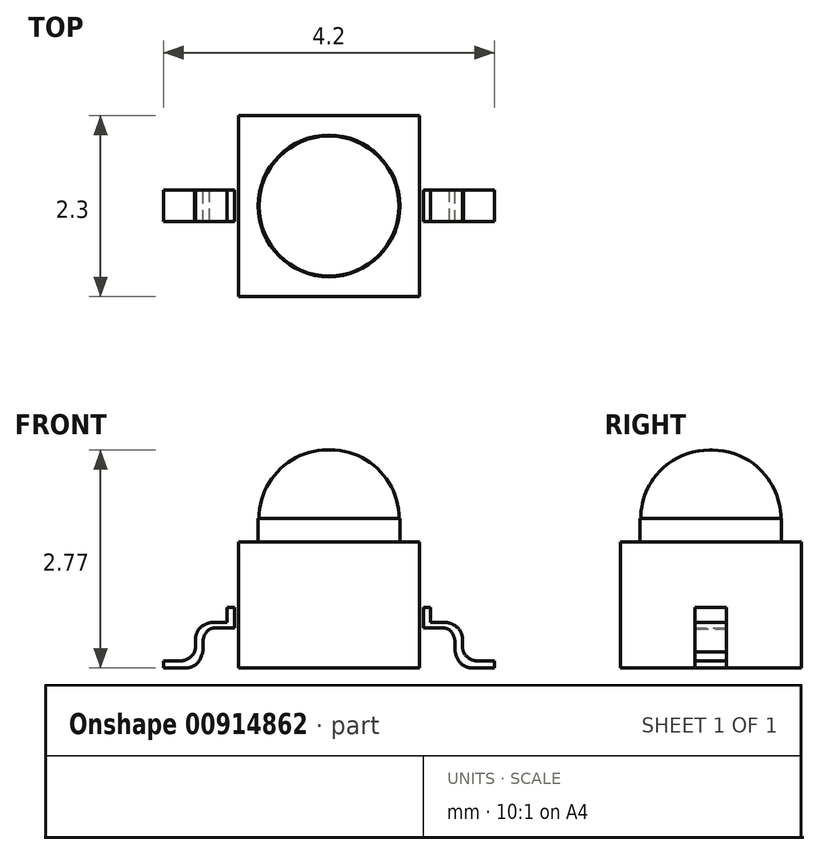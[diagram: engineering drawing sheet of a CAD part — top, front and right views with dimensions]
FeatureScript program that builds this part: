
annotation { "Feature Type Name" : "Feature", "Feature Type Description" : "" }
export const myFeature = defineFeature(function(context is Context, id is Id, definition is map)
    precondition{}
    {
        {
            var Q0;
            Q0=qCreatedBy(makeId("Top.planeOp"),FACE);
            var sketch = newSketch(context, id + "F0", { "sketchPlane" : qUnion([Q0])});
            skLineSegment(sketch, "E0.bottom", {"start": v(-1.15, 1.15) * mm, "end": v(1.15, 1.15) * mm});
            skLineSegment(sketch, "E0.top", {"start": v(-1.15, -1.15) * mm, "end": v(1.15, -1.15) * mm});
            skLineSegment(sketch, "E0.left", {"start": v(-1.15, 1.15) * mm, "end": v(-1.15, -1.15) * mm});
            skLineSegment(sketch, "E0.right", {"start": v(1.15, 1.15) * mm, "end": v(1.15, -1.15) * mm});
            skPoint(sketch, "E0.middle", {"position": v(0, 0) * mm});
            skSolve(sketch);
        }
        {
            var Q0;
            Q0 = qSketchRegion(id + "F0", true);
            extrude(context, id + "F1", {"entities" : qUnion([Q0]), "depth" : 1.6 * mm, "offsetDistance" : 25.4 * mm});
        }
        {
            var Q0;
            Q0=makeQuery(id+"F1.opExtrude","CAP_FACE",FACE,{"disambiguationData":[OSD([sQuery(id+"F0.wireOp",EDGE,"E0.bottom"),sQuery(id+"F0.wireOp",EDGE,"E0.top"),sQuery(id+"F0.wireOp",EDGE,"E0.left"),sQuery(id+"F0.wireOp",EDGE,"E0.right")])],"isStart":false});
            var sketch = newSketch(context, id + "F2", { "sketchPlane" : qUnion([Q0])});
            skCircle(sketch, "E1", {"center": v(0, 0) * mm, "radius": 0.9 * mm});
            skSolve(sketch);
        }
        {
            var Q0;
            Q0 = qSketchRegion(id + "F2", true);
            extrude(context, id + "F3", {"entities" : qUnion([Q0]), "operationType" : NewBodyOperationType.ADD, "depth" : 0.3 * mm, "offsetDistance" : 25.4 * mm});
        }
        {
            var Q0;
            Q0=makeQuery(id+"F3.opExtrude","CAP_FACE",FACE,{"disambiguationData":[OSD([sQuery(id+"F2.wireOp",EDGE,"E1")])],"isStart":false});
            var sketch = newSketch(context, id + "F4", { "sketchPlane" : qUnion([Q0])});
            skCircle(sketch, "E2", {"center": v(0, 0) * mm, "radius": 0.89 * mm});
            skSolve(sketch);
        }
        {
            var Q0;
            Q0 = qSketchRegion(id + "F4", true);
            extrude(context, id + "F5", {"entities" : qUnion([Q0]), "operationType" : NewBodyOperationType.ADD, "depth" : 0.87 * mm, "offsetDistance" : 25.4 * mm});
        }
        {
            var Q0;
            Q0=makeQuery(id+"F5.opExtrude","CAP_EDGE",EDGE,{"disambiguationData":[OSD([sQuery(id+"F4.wireOp",EDGE,"E2")])],"isStart":false});
            fillet(context, id + "F6", {"entities" : qUnion([Q0]), "radius" : 0.87 * mm, "tangentPropagation" : true, "allowEdgeOverflow" : false});
        }
        {
            var Q0;
            Q0=qCreatedBy(makeId("Front.planeOp"),FACE);
            var sketch = newSketch(context, id + "F7", { "sketchPlane" : qUnion([Q0])});
            skLineSegment(sketch, "E3", {"start": v(-1.2, 0.77) * mm, "end": v(-1.2, 0.51) * mm});
            skLineSegment(sketch, "E4", {"start": v(-1.2, 0.51) * mm, "end": v(-1.5, 0.51) * mm});
            skLineSegment(sketch, "E5", {"start": v(-1.5, 0.51) * mm, "end": v(-1.6, 0.44) * mm});
            skLineSegment(sketch, "E6", {"start": v(-1.6, 0.44) * mm, "end": v(-1.6, 0.2) * mm});
            skLineSegment(sketch, "E7", {"start": v(-1.6, 0.2) * mm, "end": v(-1.68, 0) * mm});
            skLineSegment(sketch, "E8", {"start": v(-1.68, 0) * mm, "end": v(-2.1, 0) * mm});
            skLineSegment(sketch, "E9", {"start": v(-2.1, 0) * mm, "end": v(-2.1, 0.1) * mm});
            skLineSegment(sketch, "E10", {"start": v(-2.1, 0.1) * mm, "end": v(-1.76, 0.1) * mm});
            skLineSegment(sketch, "E11", {"start": v(-1.76, 0.1) * mm, "end": v(-1.7, 0.24) * mm});
            skLineSegment(sketch, "E12", {"start": v(-1.7, 0.24) * mm, "end": v(-1.7, 0.48) * mm});
            skLineSegment(sketch, "E13", {"start": v(-1.7, 0.48) * mm, "end": v(-1.53, 0.58) * mm});
            skLineSegment(sketch, "E14", {"start": v(-1.53, 0.58) * mm, "end": v(-1.3, 0.58) * mm});
            skLineSegment(sketch, "E15", {"start": v(-1.3, 0.58) * mm, "end": v(-1.3, 0.77) * mm});
            skLineSegment(sketch, "E16", {"start": v(-1.3, 0.77) * mm, "end": v(-1.2, 0.77) * mm});
            skSolve(sketch);
        }
        {
            var Q0;
            Q0 = qSketchRegion(id + "F7", true);
            extrude(context, id + "F8", {"entities" : qUnion([Q0]), "endBound" : BoundingType.SYMMETRIC, "depth" : 0.4 * mm, "offsetDistance" : 25.4 * mm});
        }
        {
            var Q0;
            Q0=makeQuery(id+"F8.opExtrude","SWEPT_EDGE",EDGE,{"disambiguationData":[OSD([sQuery(id+"F7.wireOp",EDGE,"E12"),sQuery(id+"F7.wireOp",EDGE,"E13")])]});
            var Q1;
            Q1=makeQuery(id+"F8.opExtrude","SWEPT_EDGE",EDGE,{"disambiguationData":[OSD([sQuery(id+"F7.wireOp",EDGE,"E13"),sQuery(id+"F7.wireOp",EDGE,"E14")])]});
            var Q2;
            Q2=makeQuery(id+"F8.opExtrude","SWEPT_EDGE",EDGE,{"disambiguationData":[OSD([sQuery(id+"F7.wireOp",EDGE,"E6"),sQuery(id+"F7.wireOp",EDGE,"E7")])]});
            var Q3;
            Q3=makeQuery(id+"F8.opExtrude","SWEPT_EDGE",EDGE,{"disambiguationData":[OSD([sQuery(id+"F7.wireOp",EDGE,"E7"),sQuery(id+"F7.wireOp",EDGE,"E8")])]});
            fillet(context, id + "F9", {"entities" : qUnion([Q0, Q1, Q2, Q3]), "radius" : 0.2 * mm, "tangentPropagation" : true, "allowEdgeOverflow" : false});
        }
        {
            var Q0;
            Q0=makeQuery(id+"F8.opExtrude","SWEPT_EDGE",EDGE,{"disambiguationData":[OSD([sQuery(id+"F7.wireOp",EDGE,"E10"),sQuery(id+"F7.wireOp",EDGE,"E11")])]});
            var Q1;
            Q1=makeQuery(id+"F8.opExtrude","SWEPT_EDGE",EDGE,{"disambiguationData":[OSD([sQuery(id+"F7.wireOp",EDGE,"E11"),sQuery(id+"F7.wireOp",EDGE,"E12")])]});
            var Q2;
            Q2=makeQuery(id+"F8.opExtrude","SWEPT_EDGE",EDGE,{"disambiguationData":[OSD([sQuery(id+"F7.wireOp",EDGE,"E5"),sQuery(id+"F7.wireOp",EDGE,"E6")])]});
            var Q3;
            Q3=makeQuery(id+"F8.opExtrude","SWEPT_EDGE",EDGE,{"disambiguationData":[OSD([sQuery(id+"F7.wireOp",EDGE,"E4"),sQuery(id+"F7.wireOp",EDGE,"E5")])]});
            fillet(context, id + "F10", {"entities" : qUnion([Q0, Q1, Q2, Q3]), "radius" : 0.2 * mm, "tangentPropagation" : true, "allowEdgeOverflow" : false});
        }
        {
            var Q0;
            Q0=makeQuery(id+"F8.opExtrude","SWEPT_BODY",BODY,{"disambiguationData":[OSD([sQuery(id+"F7.wireOp",EDGE,"E3"),sQuery(id+"F7.wireOp",EDGE,"E4"),sQuery(id+"F7.wireOp",EDGE,"E5"),sQuery(id+"F7.wireOp",EDGE,"E6"),sQuery(id+"F7.wireOp",EDGE,"E7"),sQuery(id+"F7.wireOp",EDGE,"E8"),sQuery(id+"F7.wireOp",EDGE,"E9"),sQuery(id+"F7.wireOp",EDGE,"E10"),sQuery(id+"F7.wireOp",EDGE,"E11"),sQuery(id+"F7.wireOp",EDGE,"E12"),sQuery(id+"F7.wireOp",EDGE,"E13"),sQuery(id+"F7.wireOp",EDGE,"E14"),sQuery(id+"F7.wireOp",EDGE,"E15"),sQuery(id+"F7.wireOp",EDGE,"E16")])]});
            var Q1;
            Q1=qCreatedBy(makeId("Right.planeOp"),FACE);
            mirror(context, id + "F11", {"entities" : qUnion([Q0]), "mirrorPlane" : qUnion([Q1])});
        }
    });
